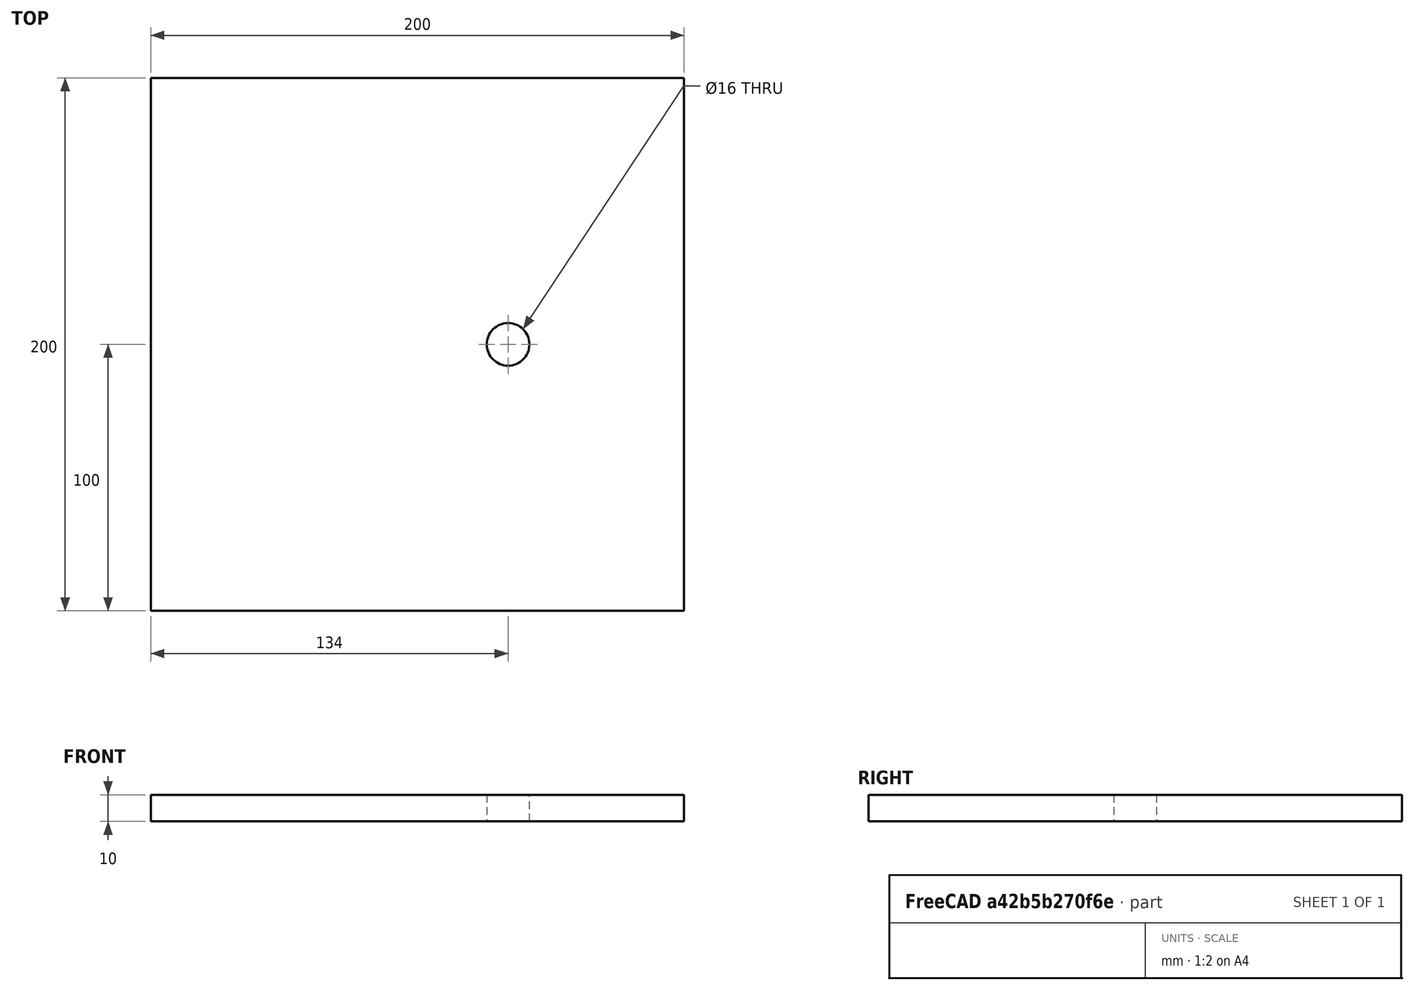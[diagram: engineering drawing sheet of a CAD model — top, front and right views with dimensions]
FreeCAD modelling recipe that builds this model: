
FCSTD DOCUMENT  (FreeCAD 0.19R24276 (Git))
Label: bldc_holder_p1_200x200x10_otv
License: All rights reserved
LicenseURL: http://en.wikipedia.org/wiki/All_rights_reserved
objects: Sketcher::SketchObject×1, PartDesign::Pad×1, PartDesign::Body×1
note: 4 computed .brp shape members not serialized (recipe doc carries the construction recipe); baked Part::Feature solids carry a one-line shape summary decoded from their .brp

FEATURE [Sketcher::SketchObject] Sketch
  FullyConstrained = true
  MapMode = 5
  Support = -> [XY_Plane]
  sketch-geometry (6):
    g0: LineSegment StartX=0 StartY=0 StartZ=0 EndX=200 EndY=0 EndZ=0
    g1: LineSegment StartX=200 StartY=0 StartZ=0 EndX=200 EndY=200 EndZ=0
    g2: LineSegment StartX=200 StartY=200 StartZ=0 EndX=0 EndY=200 EndZ=0
    g3: LineSegment StartX=0 StartY=200 StartZ=0 EndX=0 EndY=0 EndZ=0
    g4: Circle CenterX=134 CenterY=100 CenterZ=0 NormalX=0 NormalY=0 NormalZ=1 AngleXU=0 Radius=8
    g5: Circle CenterX=134 CenterY=100 CenterZ=0 NormalX=0 NormalY=0 NormalZ=1 AngleXU=0 Radius=65.5
  constraints (16):
    c: Coincident(g0,g1)
    c: Coincident(g1,g2)
    c: Coincident(g2,g3)
    c: Coincident(g3,g0)
    c: Horizontal(g0)
    c: Horizontal(g2)
    c: Vertical(g1)
    c: Vertical(g3)
    c: Coincident(g0,g-1)
    c: Equal(g1,g2)
    c: DistanceX(g0,g0) = 200
    c: Coincident(g5,g4)
    c: Diameter(g5) = 131
    c: DistanceX(g4,g1) = 66
    c: DistanceY(g0,g4) = 100
    c: Diameter(g4) = 16
FEATURE [PartDesign::Pad] Pad
  Direction = (1,1,1)
  Length = 10
  Length2 = 100
  Profile = -> Sketch
  Type = 0
FEATURE [PartDesign::Body] Body
  Group = -> [Sketch,Pad]
  Origin = -> Origin
  Tip = -> Pad
